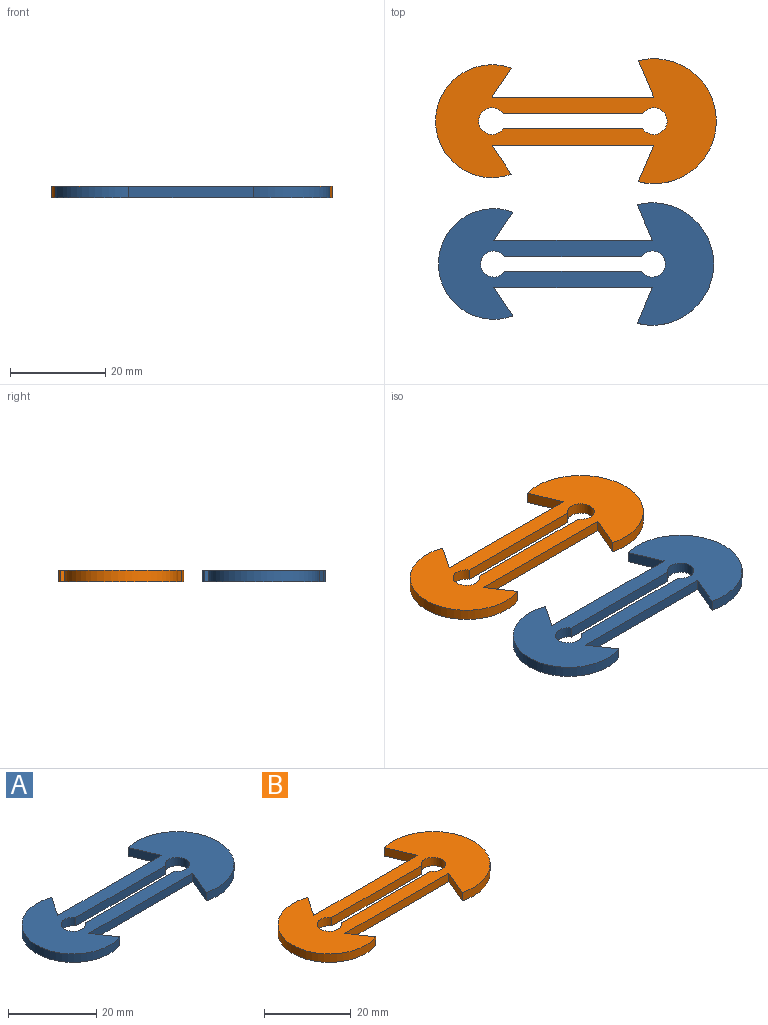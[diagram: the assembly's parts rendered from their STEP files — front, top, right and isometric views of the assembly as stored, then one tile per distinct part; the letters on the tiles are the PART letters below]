
ASSEMBLY  parts=2 mates=1
PART A: 14 faces, bbox 57.8x25.8x2.3 mm
  f0: plane 28.72x2.33mm, normal (0,-1,0), area 66.9mm2, adj f10,f11,f12,f13
  f1: plane 28.72x2.33mm, normal (0,1,0), area 66.9mm2, adj f10,f11,f12,f13
  f2: plane 33.32x2.33mm, normal (0,1,0), area 77.6mm2, adj f3,f9,f10,f11
  f3: plane 5.94x3.98mm, normal (0.83,-0.56,0), area 16.7mm2, adj f2,f4,f10,f11
  f4: cylinder r=11.62mm len=23.25mm, axis (0,0,-1), area 104mm2, adj f3,f5,f10,f11
  f5: plane 5.94x3.98mm, normal (0.83,0.56,0), area 16.7mm2, adj f4,f6,f10,f11
  f6: plane 33.32x2.33mm, normal (0,-1,0), area 77.6mm2, adj f5,f7,f10,f11
  f7: plane 7.49x3.2mm, normal (-0.92,0.39,0), area 19mm2, adj f6,f8,f10,f11
  f8: cylinder r=12.88mm len=25.75mm, axis (0,0,-1), area 109.3mm2, adj f7,f9,f10,f11
  f9: plane 7.49x3.2mm, normal (-0.92,-0.39,0), area 19mm2, adj f2,f8,f10,f11
  f10: plane 57.82x25.75mm, normal (0,0,1), area 725.3mm2, adj f0,f1,f2,f3,f4,f5,f6,f7
  f11: plane 57.82x25.75mm, normal (0,0,-1), area 725.3mm2, adj f0,f1,f2,f3,f4,f5,f6,f7
  f12: cylinder r=2.75mm len=5.5mm, axis (0,0,-1), area 32.8mm2, adj f0,f1,f10,f11
  f13: cylinder r=2.75mm len=5.5mm, axis (0,0,-1), area 32.8mm2, adj f0,f1,f10,f11
PART B: 14 faces, bbox 59x26.3x2.4 mm
  f0: plane 29.3x2.38mm, normal (0,-1,0), area 69.6mm2, adj f10,f11,f12,f13
  f1: plane 29.3x2.38mm, normal (0,1,0), area 69.6mm2, adj f10,f11,f12,f13
  f2: plane 33.99x2.38mm, normal (0,1,0), area 80.8mm2, adj f3,f9,f10,f11
  f3: plane 6.06x4.06mm, normal (0.83,-0.56,0), area 17.3mm2, adj f2,f4,f10,f11
  f4: cylinder r=11.86mm len=23.72mm, axis (0,0,-1), area 108.2mm2, adj f3,f5,f10,f11
  f5: plane 6.06x4.06mm, normal (0.83,0.56,0), area 17.3mm2, adj f4,f6,f10,f11
  f6: plane 33.99x2.38mm, normal (0,-1,0), area 80.8mm2, adj f5,f7,f10,f11
  f7: plane 7.64x3.26mm, normal (-0.92,0.39,0), area 19.7mm2, adj f6,f8,f10,f11
  f8: cylinder r=13.13mm len=26.27mm, axis (0,0,-1), area 113.7mm2, adj f7,f9,f10,f11
  f9: plane 7.64x3.26mm, normal (-0.92,-0.39,0), area 19.7mm2, adj f2,f8,f10,f11
  f10: plane 58.98x26.27mm, normal (0,0,1), area 754.6mm2, adj f0,f1,f2,f3,f4,f5,f6,f7
  f11: plane 58.98x26.27mm, normal (0,0,-1), area 754.6mm2, adj f0,f1,f2,f3,f4,f5,f6,f7
  f12: cylinder r=2.81mm len=5.61mm, axis (0,0,-1), area 34.1mm2, adj f0,f1,f10,f11
  f13: cylinder r=2.81mm len=5.61mm, axis (0,0,-1), area 34.1mm2, adj f0,f1,f10,f11
PLACE A t=(-46.8,14.08,0.01)mm
PLACE B t=(-47.17,74.11,0.01)mm
MATE planar A.f11 <-> B.f11  axis (0,0,-1) through (-28.55,14.08,0.01)mm
